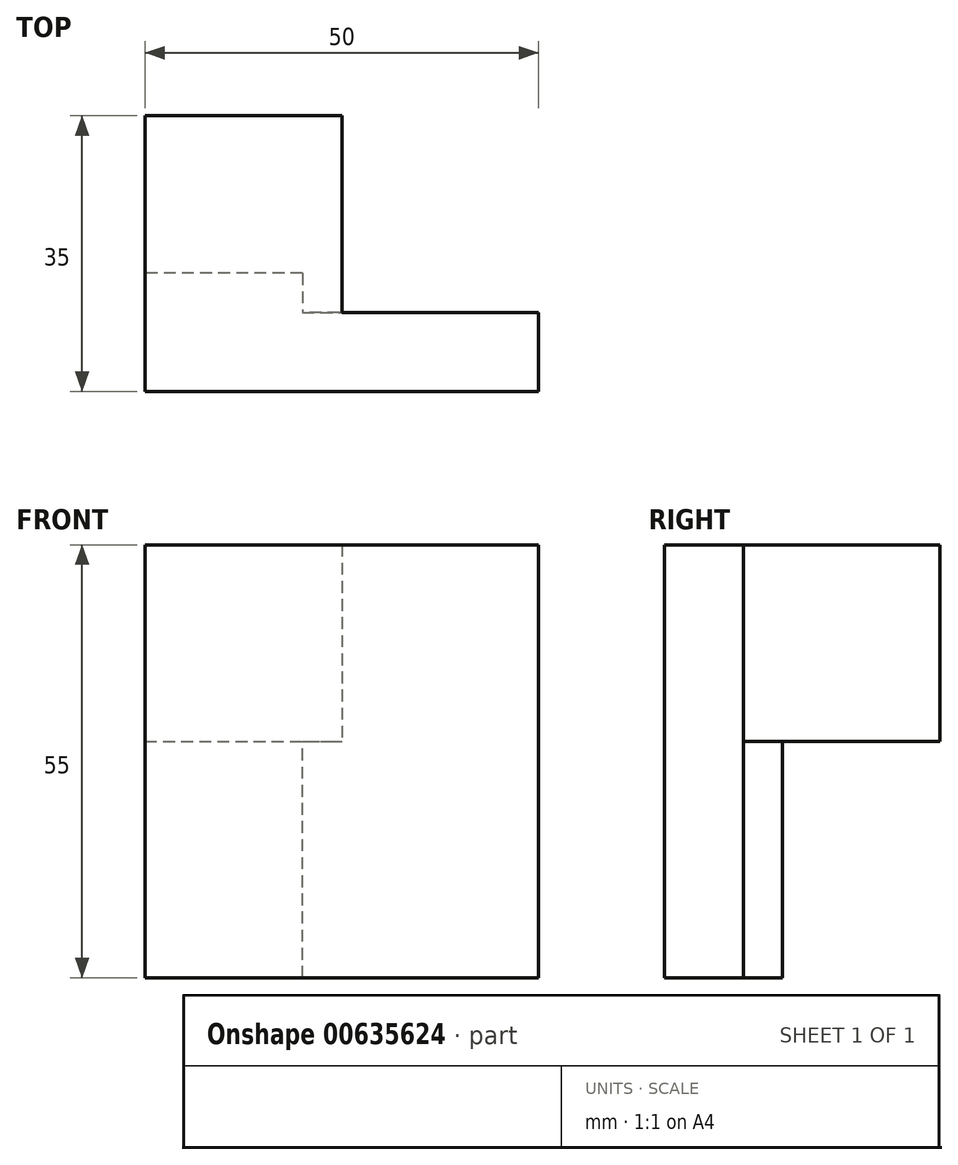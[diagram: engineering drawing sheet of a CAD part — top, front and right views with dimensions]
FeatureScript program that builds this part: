
annotation { "Feature Type Name" : "Feature", "Feature Type Description" : "" }
export const myFeature = defineFeature(function(context is Context, id is Id, definition is map)
    precondition{}
    {
        {
            var Q0;
            Q0=qCreatedBy(makeId("Front.planeOp"),FACE);
            var sketch = newSketch(context, id + "F0", { "sketchPlane" : qUnion([Q0])});
            skLineSegment(sketch, "E0.bottom", {"start": v(25, 27.5) * mm, "end": v(-25, 27.5) * mm});
            skLineSegment(sketch, "E0.top", {"start": v(25, -27.5) * mm, "end": v(-25, -27.5) * mm});
            skLineSegment(sketch, "E0.left", {"start": v(25, 27.5) * mm, "end": v(25, -27.5) * mm});
            skLineSegment(sketch, "E0.right", {"start": v(-25, 27.5) * mm, "end": v(-25, -27.5) * mm});
            skPoint(sketch, "E0.middle", {"position": v(0, 0) * mm});
            skSolve(sketch);
        }
        {
            var Q0;
            Q0 = qSketchRegion(id + "F0", true);
            extrude(context, id + "F1", {"entities" : qUnion([Q0]), "depth" : 10 * mm, "offsetDistance" : 25 * mm});
        }
        {
            var Q0;
            Q0=makeQuery(id+"F1.opExtrude","CAP_FACE",FACE,{"disambiguationData":[OSD([sQuery(id+"F0.wireOp",EDGE,"E0.bottom"),sQuery(id+"F0.wireOp",EDGE,"E0.top"),sQuery(id+"F0.wireOp",EDGE,"E0.left"),sQuery(id+"F0.wireOp",EDGE,"E0.right")])],"isStart":true});
            var sketch = newSketch(context, id + "F2", { "sketchPlane" : qUnion([Q0])});
            skLineSegment(sketch, "E1.bottom", {"start": v(25, 27.5) * mm, "end": v(0, 27.5) * mm});
            skLineSegment(sketch, "E1.top", {"start": v(25, 2.5) * mm, "end": v(0, 2.5) * mm});
            skLineSegment(sketch, "E1.left", {"start": v(25, 27.5) * mm, "end": v(25, 2.5) * mm});
            skLineSegment(sketch, "E1.right", {"start": v(0, 27.5) * mm, "end": v(0, 2.5) * mm});
            skSolve(sketch);
        }
        {
            var Q0;
            Q0 = qSketchRegion(id + "F2", true);
            extrude(context, id + "F3", {"entities" : qUnion([Q0]), "operationType" : NewBodyOperationType.ADD, "depth" : 25 * mm, "offsetDistance" : 25 * mm});
        }
        {
            var Q0;
            Q0=makeQuery(id+"F1.opExtrude","CAP_FACE",FACE,{"disambiguationData":[OSD([sQuery(id+"F0.wireOp",EDGE,"E0.bottom"),sQuery(id+"F0.wireOp",EDGE,"E0.top"),sQuery(id+"F0.wireOp",EDGE,"E0.left"),sQuery(id+"F0.wireOp",EDGE,"E0.right")])],"isStart":true});
            var sketch = newSketch(context, id + "F4", { "sketchPlane" : qUnion([Q0])});
            skLineSegment(sketch, "E2.bottom", {"start": v(25, -27.5) * mm, "end": v(5, -27.5) * mm});
            skLineSegment(sketch, "E2.top", {"start": v(25, 2.5) * mm, "end": v(5, 2.5) * mm});
            skLineSegment(sketch, "E2.left", {"start": v(25, -27.5) * mm, "end": v(25, 2.5) * mm});
            skLineSegment(sketch, "E2.right", {"start": v(5, -27.5) * mm, "end": v(5, 2.5) * mm});
            skSolve(sketch);
        }
        {
            var Q0;
            Q0 = qSketchRegion(id + "F4", true);
            extrude(context, id + "F5", {"entities" : qUnion([Q0]), "operationType" : NewBodyOperationType.ADD, "depth" : 5 * mm, "offsetDistance" : 25 * mm});
        }
    });
